# Revit family: Power-ModularDevices-GEWISS-90AM-CONTACTORS_20A_1M
name_source: partatom
category: Apparecchi elettrici
revit_build: Autodesk Revit 2016 (Build: 20161004_0715(x64)
units: mm (PartAtom-declared; Revit-internal decimal feet)

## family parameters
Condiviso = No
Host = Superficie
Mantenere orientamento annotazione = Sì
Numero OmniClass = 23.80.30.00
Punto di calcolo locali = Sì
Quota connettore circolare = Usa diametro
Taglio con vuoti quando caricato = No
Tipo di parte = Normale
Titolo OmniClass = Distribution Devices

## types (6) — shared parameters
A = 9 mm  [stored 0.0295276 ft]
B = 85 mm  [stored 0.278871 ft]
C = 65 mm  [stored 0.213255 ft]
Catalogue = POWER
Catalogue Range = 90 AM
D = 45 mm  [stored 0.147638 ft]
Electrocod = 1712
Fin_Amperometro = <Per categoria>
IDF = baf2400b-6567-46ca-9c69-fbc974be7a5d
IDT = ec2c330b-f530-4fc0-b450-a6db8886eae5
Immagine tipo = GWD6707.jpg
No. Chorus modules = 1
Numero poli = 1
Potenza in Watt = 0 V
Produttore = GEWISS S.p.A.
Prospetto di default = 1219 mm
Rated current (AC-1/AC-7a) = 20 A - CTR20
TEXT LABEL = A
Technical sheet = https://www.gewiss.com
URL = https://www.gewiss.com
Version file RFA = 18.0

## per-type parameters (varying)
| type | Control coil voltage (V) | Descrizione | EAN code | Modello |
| GWD6701 - CONTACTOR 20A 1NO 230V 1M | 230Vac | CONTACTOR 20A 1NO 230V 1M | 8011564809314 | GWD6701 |
| GWD6707 - CONTACTOR 20A 1NO+1NC 230V 1M | 230Vac | CONTACTOR 20A 1NO+1NC 230V 1M | 8011564809376 | GWD6707 |
| GWD6705 - CONTACTOR 2NC 20A 230V 1M | 230Vac | CONTACTOR 2NC 20A 230V 1M | 8011564809352 | GWD6705 |
| GWD6703 - CONTACTOR 20A 2NO 230V 1M | 230Vac | CONTACTOR 20A 2NO 230V 1M | 8011564809338 | GWD6703 |
| GWD6706 - CONTACTOR 20A 1NO+1NC 24V 1M | 24Vac | CONTACTOR 20A 1NO+1NC 24V 1M | 8011564809369 | GWD6706 |
| GWD6702 - CONTACTOR 20A 2NO 24V 1M | 24Vac | CONTACTOR 20A 2NO 24V 1M | 8011564809321 | GWD6702 |

note: [stored X ft] marks values corroborated as IEEE doubles in the binary element streams (Revit-internal decimal feet)
